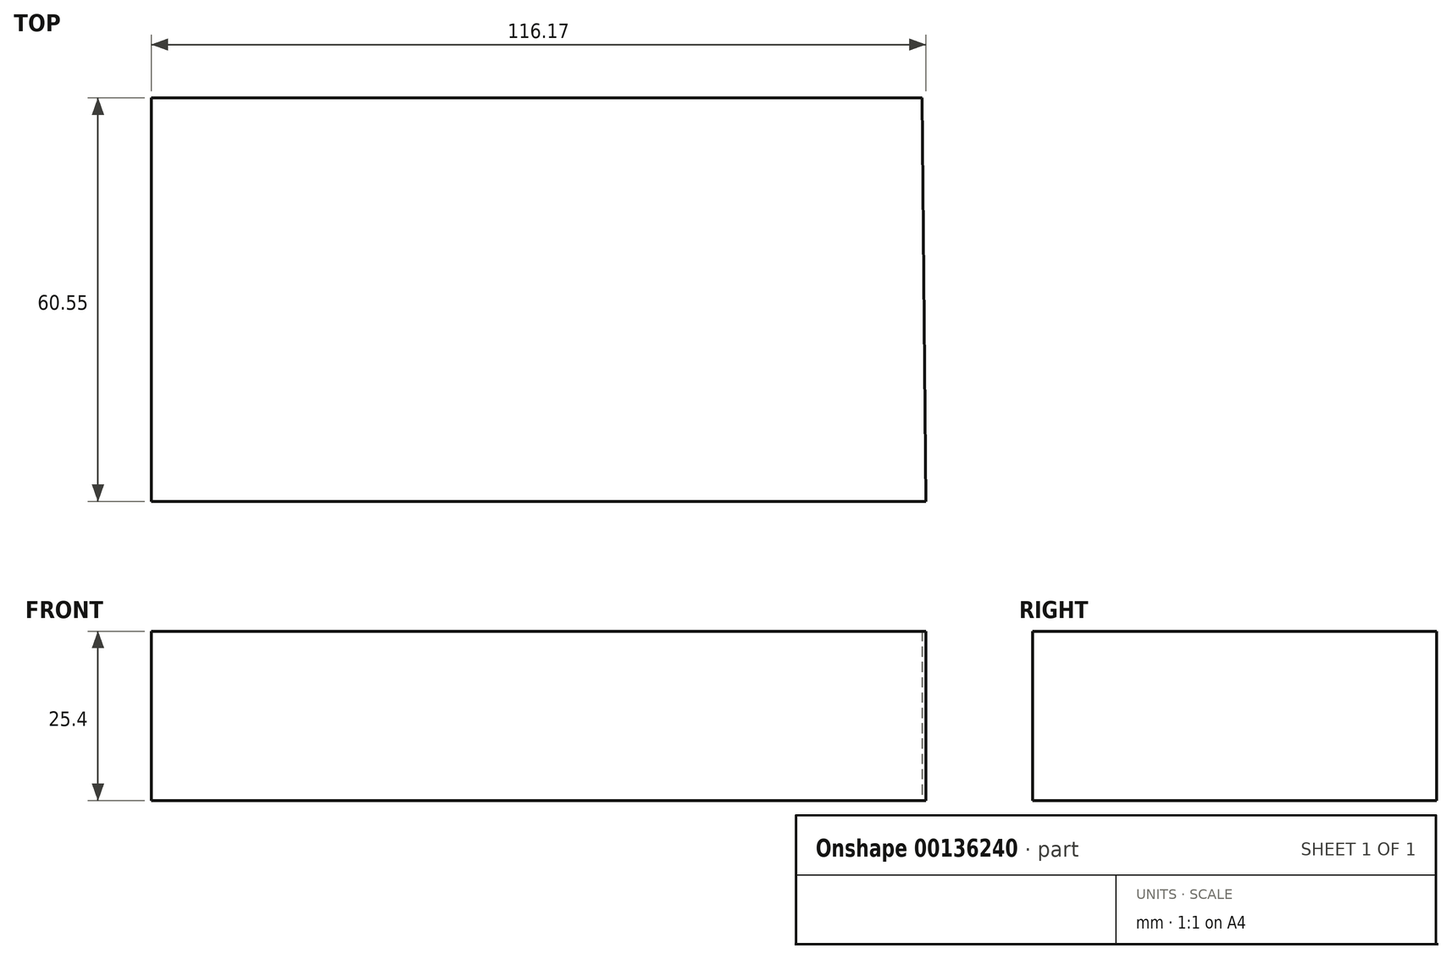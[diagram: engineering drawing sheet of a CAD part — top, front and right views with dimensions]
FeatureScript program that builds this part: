
annotation { "Feature Type Name" : "Feature", "Feature Type Description" : "" }
export const myFeature = defineFeature(function(context is Context, id is Id, definition is map)
    precondition{}
    {
        {
            var Q0;
            Q0=qCreatedBy(makeId("Top.planeOp"),FACE);
            var sketch = newSketch(context, id + "F0", { "sketchPlane" : qUnion([Q0])});
            skLineSegment(sketch, "E0", {"start": v(-61.7, 42.8) * mm, "end": v(53.9, 42.8) * mm});
            skLineSegment(sketch, "E1", {"start": v(-61.7, 42.8) * mm, "end": v(-61.7, -17.75) * mm});
            skLineSegment(sketch, "E2", {"start": v(54.48, -17.75) * mm, "end": v(-61.7, -17.75) * mm});
            skLineSegment(sketch, "E3", {"start": v(53.9, 42.8) * mm, "end": v(54.48, -17.75) * mm});
            skSolve(sketch);
        }
        {
            var Q0;
            Q0 = qSketchRegion(id + "F0", true);
            extrude(context, id + "F1", {"entities" : qUnion([Q0]), "depth" : 25.4 * mm});
        }
    });
